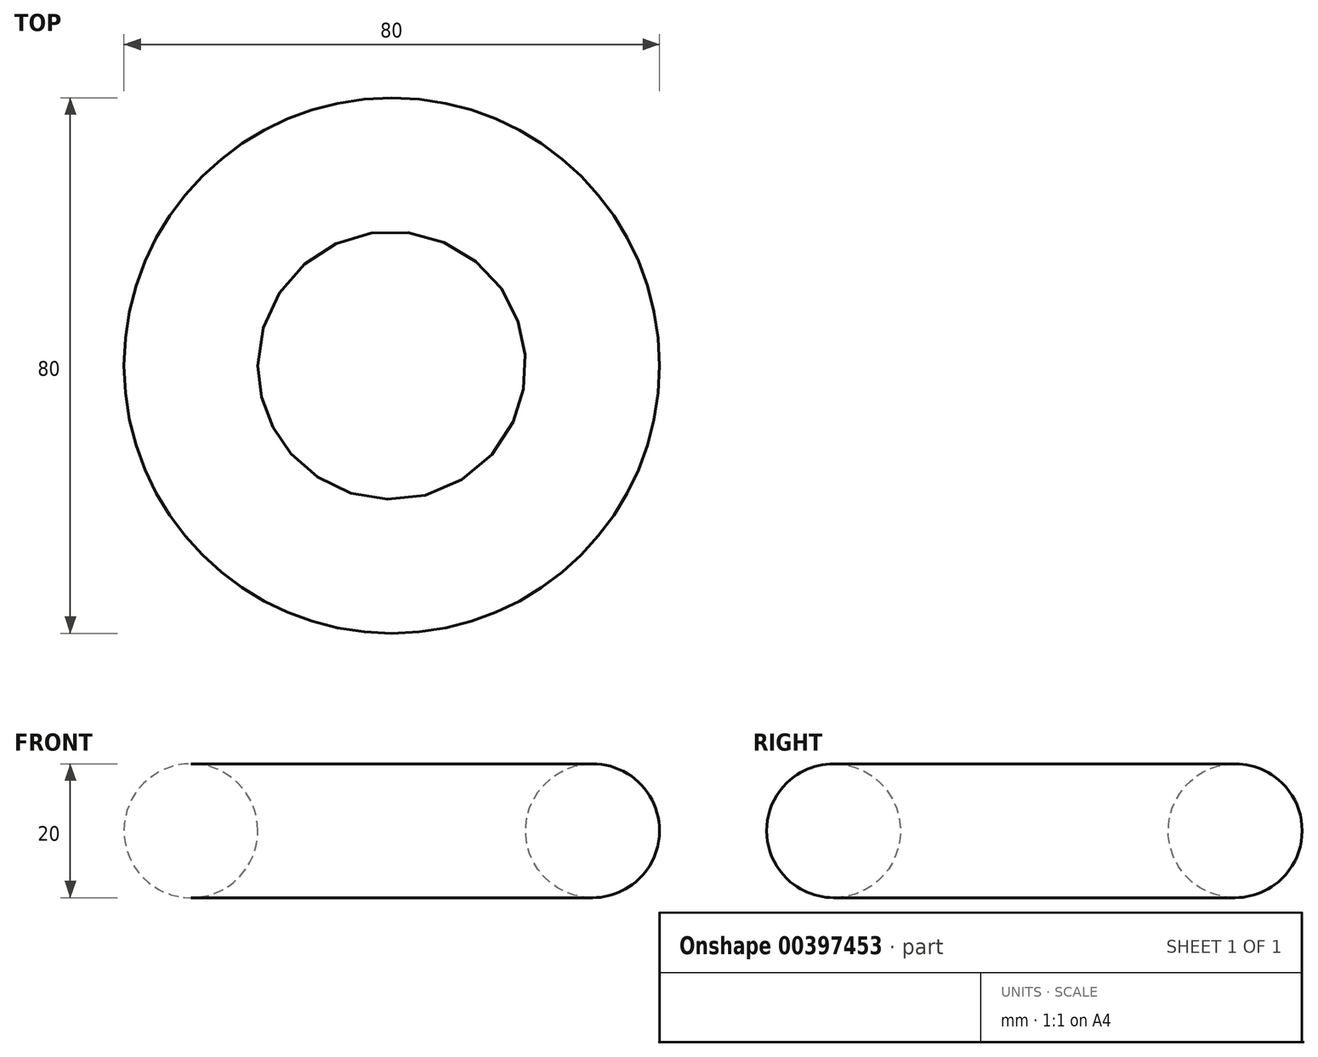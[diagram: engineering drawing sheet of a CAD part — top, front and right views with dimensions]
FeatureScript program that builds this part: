
annotation { "Feature Type Name" : "Feature", "Feature Type Description" : "" }
export const myFeature = defineFeature(function(context is Context, id is Id, definition is map)
    precondition{}
    {
        {
            var Q0;
            Q0=qCreatedBy(makeId("Top.planeOp"),FACE);
            var sketch = newSketch(context, id + "F0", { "sketchPlane" : qUnion([Q0])});
            skCircle(sketch, "E0", {"center": v(0, 0) * mm, "radius": 30 * mm});
            skSolve(sketch);
        }
        {
            var Q0;
            Q0=qCreatedBy(makeId("Front.planeOp"),FACE);
            var sketch = newSketch(context, id + "F1", { "sketchPlane" : qUnion([Q0])});
            skCircle(sketch, "E1", {"center": v(-30, 0) * mm, "radius": 10 * mm});
            skSolve(sketch);
        }
        {
            var Q0;
            Q0=makeQuery(id+"F1.imprint","IMPRINT",FACE,{"disambiguationData":[TD([[makeQuery(id+"F1.imprint","IMPRINT",EDGE,{"derivedFrom":sQuery(id+"F1.wireOp",EDGE,"E1")}),1.0]])]});
            var Q1;
            Q1=sQuery(id+"F0.wireOp",EDGE,"E0");
            revolve(context, id + "F2", {"surfaceOperationType" : NewSurfaceOperationType.NEW, "entities" : qUnion([Q0]), "axis" : qUnion([Q1]), "revolveType" : RevolveType.FULL});
        }
    });
